# Revit family: WC OLIMPIA RCH 2
name_source: partatom
category: Plumbing Fixtures
revit_build: Autodesk Revit 2015 (Build: 20140223_1515(x64)
units: mm (PartAtom-declared; Revit-internal decimal feet)

## types (1)
- TTR
    Certification = http://helvex.com
    Compliance = NOM-009-CONAGUA-2001
    Data Sheet = http://helvex.com
    Description = 1 gpf Olimpia Discharge Spaces Reduced Ecological With Exposed Trapway
    Features = Sleek Ergonomic Design; Maximum Efficiency; Flat Base; Sturdy Built; Premium Quality High Gloss (A); Exposed Glazed Trapway; Siphon Action Jetted Bowl; Optimum Water Surface; Certified Intake And Flushing Valves; Silent Intake Valve; Sealed Flushing Valve; Flush Valve With Seal; Setting Kit Included; 5-Yr Warranty In Iron Fittings; Saves On Water Consumption; Less Than 1 gpf Consumption
    High Gloss Ceramic = High Gloss Ceramic
    Inlet Threads = Feeding: Ø15/16" - 14 NS - 1;  Flush: Couple With Sanitary Flange
    Instructive = http://helvex.com
    Manufacturer = HELVEX
    Max. Working Pressure = 85.3 psi
    Maximum Consumption = 1.00 gpf
    Min. Working Pressure = 3.5 psi
    Model = TTR
    Total Height = 30"
    Total Length = 26"
    Total Width = 15"
    Type Comments = Ceramic
    URL = http://helvex.com

## geometry (parser evidence)
native form markers: Sweep x3
no freeform markers — native parametric forms only
